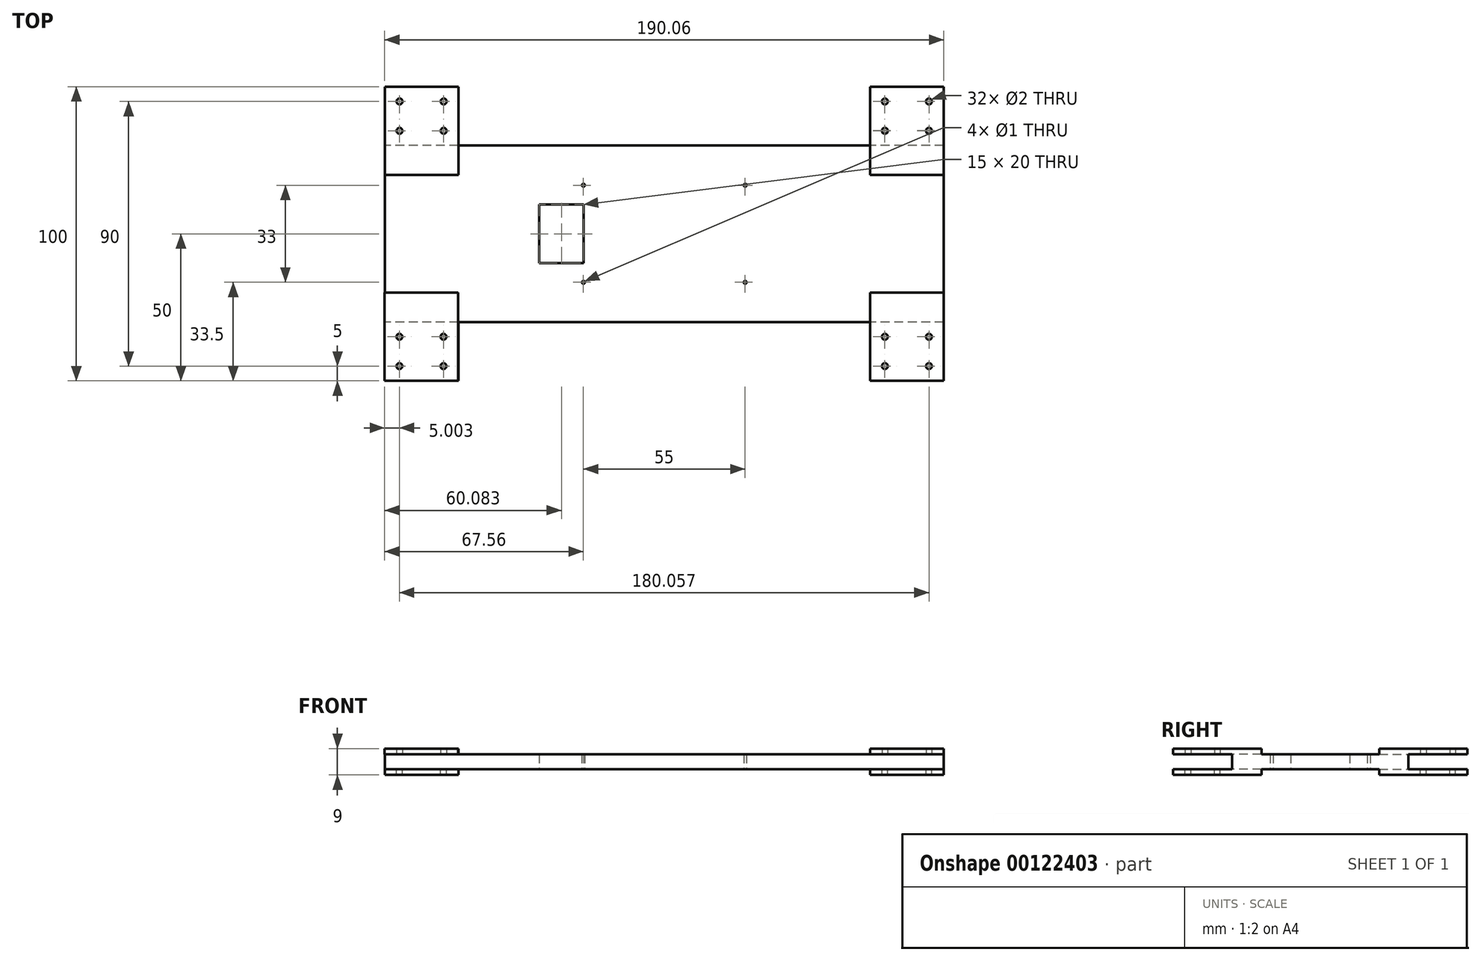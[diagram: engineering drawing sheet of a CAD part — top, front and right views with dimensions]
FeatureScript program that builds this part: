
annotation { "Feature Type Name" : "Feature", "Feature Type Description" : "" }
export const myFeature = defineFeature(function(context is Context, id is Id, definition is map)
    precondition{}
    {
        {
            var Q0;
            Q0=qCreatedBy(makeId("Top.planeOp"),FACE);
            var sketch = newSketch(context, id + "F0", { "sketchPlane" : qUnion([Q0])});
            skLineSegment(sketch, "E0.bottom", {"start": v(95, -30) * mm, "end": v(-95, -30) * mm});
            skLineSegment(sketch, "E0.top", {"start": v(95, 30) * mm, "end": v(-95, 30) * mm});
            skLineSegment(sketch, "E0.left", {"start": v(95, -30) * mm, "end": v(95, 30) * mm});
            skLineSegment(sketch, "E0.right", {"start": v(-95, -30) * mm, "end": v(-95, 30) * mm});
            skPoint(sketch, "E0.middle", {"position": v(0, 0) * mm});
            skLineSegment(sketch, "E1.bottom", {"start": v(27.5, -16.5) * mm, "end": v(-27.5, -16.5) * mm});
            skLineSegment(sketch, "E1.top", {"start": v(27.5, 16.5) * mm, "end": v(-27.5, 16.5) * mm});
            skLineSegment(sketch, "E1.left", {"start": v(27.5, -16.5) * mm, "end": v(27.5, 16.5) * mm});
            skLineSegment(sketch, "E1.right", {"start": v(-27.5, -16.5) * mm, "end": v(-27.5, 16.5) * mm});
            skCircle(sketch, "E2", {"center": v(-27.5, 16.5) * mm, "radius": 0.5 * mm});
            skCircle(sketch, "E3", {"center": v(27.5, 16.5) * mm, "radius": 0.5 * mm});
            skCircle(sketch, "E4", {"center": v(-27.5, -16.5) * mm, "radius": 0.5 * mm});
            skCircle(sketch, "E5", {"center": v(27.5, -16.5) * mm, "radius": 0.5 * mm});
            skLineSegment(sketch, "E6.bottom", {"start": v(-236.35, 48.21) * mm, "end": v(-211.35, 48.21) * mm});
            skLineSegment(sketch, "E6.top", {"start": v(-236.35, 108.21) * mm, "end": v(-211.35, 108.21) * mm});
            skLineSegment(sketch, "E6.left", {"start": v(-236.35, 48.21) * mm, "end": v(-236.35, 108.21) * mm});
            skLineSegment(sketch, "E6.right", {"start": v(-211.35, 48.21) * mm, "end": v(-211.35, 108.21) * mm});
            skLineSegment(sketch, "E7", {"start": v(-223.85, 108.21) * mm, "end": v(-223.85, 48.21) * mm});
            skCircle(sketch, "E8", {"center": v(-223.85, 98.21) * mm, "radius": 3 * mm});
            skCircle(sketch, "E9", {"center": v(-223.85, 98.21) * mm, "radius": 5 * mm});
            skLineSegment(sketch, "E10.bottom", {"start": v(-251.47, -12.81) * mm, "end": v(-331.47, -12.81) * mm});
            skLineSegment(sketch, "E10.top", {"start": v(-251.47, 32.19) * mm, "end": v(-331.47, 32.19) * mm});
            skLineSegment(sketch, "E10.left", {"start": v(-251.47, -12.81) * mm, "end": v(-251.47, 32.19) * mm});
            skLineSegment(sketch, "E10.right", {"start": v(-331.47, -12.81) * mm, "end": v(-331.47, 32.19) * mm});
            skLineSegment(sketch, "E11.bottom", {"start": v(-27.48, 10) * mm, "end": v(-42.48, 10) * mm});
            skLineSegment(sketch, "E11.top", {"start": v(-27.48, -10) * mm, "end": v(-42.48, -10) * mm});
            skLineSegment(sketch, "E11.left", {"start": v(-27.48, 10) * mm, "end": v(-27.48, -10) * mm});
            skLineSegment(sketch, "E11.right", {"start": v(-42.48, 10) * mm, "end": v(-42.48, -10) * mm});
            skSolve(sketch);
        }
        {
            var Q0;
            Q0=makeQuery(id+"F0.imprint","IMPRINT",FACE,{"disambiguationData":[TD([[makeQuery(id+"F0.imprint","IMPRINT",EDGE,{"derivedFrom":sQuery(id+"F0.wireOp",EDGE,"E0.bottom")}),-1.0]])]});
            var Q1;
            {var subQ10=sQuery(id+"F0.wireOp",EDGE,"E5");var subQ13=sQuery(id+"F0.wireOp",EDGE,"E1.bottom");var subQ14=makeQuery(id+"F0.imprint","INTERSECT",VERTEX,{"derivedFrom":[subQ13,subQ10]});Q1=makeQuery(id+"F0.imprint","IMPRINT",FACE,{"disambiguationData":[TD([[makeQuery(id+"F0.imprint","IMPRINT",EDGE,{"disambiguationData":[TD([[subQ14,-1.0]])],"derivedFrom":subQ13}),-1.0]])]});}
            extrude(context, id + "F1", {"entities" : qUnion([Q0, Q1]), "depth" : 5 * mm});
        }
        {
            var Q0;
            Q0=makeQuery(id+"F1.opExtrude","CAP_FACE",FACE,{"disambiguationData":[OSD([sQuery(id+"F0.wireOp",EDGE,"E0.bottom"),sQuery(id+"F0.wireOp",EDGE,"E0.top"),sQuery(id+"F0.wireOp",EDGE,"E0.left"),sQuery(id+"F0.wireOp",EDGE,"E0.right"),sQuery(id+"F0.wireOp",EDGE,"E2"),sQuery(id+"F0.wireOp",EDGE,"E3"),sQuery(id+"F0.wireOp",EDGE,"E4"),sQuery(id+"F0.wireOp",EDGE,"E5")])],"isStart":false});
            var sketch = newSketch(context, id + "F2", { "sketchPlane" : qUnion([Q0])});
            skLineSegment(sketch, "E12.bottom", {"start": v(-95, 20) * mm, "end": v(-70, 20) * mm});
            skLineSegment(sketch, "E12.top", {"start": v(-95, 50) * mm, "end": v(-70, 50) * mm});
            skLineSegment(sketch, "E12.left", {"start": v(-95, 20) * mm, "end": v(-95, 50) * mm});
            skLineSegment(sketch, "E12.right", {"start": v(-70, 20) * mm, "end": v(-70, 50) * mm});
            skLineSegment(sketch, "E13.bottom", {"start": v(-90, 45) * mm, "end": v(-75, 45) * mm});
            skLineSegment(sketch, "E13.top", {"start": v(-90, 35) * mm, "end": v(-75, 35) * mm});
            skLineSegment(sketch, "E13.left", {"start": v(-90, 45) * mm, "end": v(-90, 35) * mm});
            skLineSegment(sketch, "E13.right", {"start": v(-75, 45) * mm, "end": v(-75, 35) * mm});
            skCircle(sketch, "E14", {"center": v(-90, 45) * mm, "radius": 1 * mm});
            skCircle(sketch, "E15", {"center": v(-75, 45) * mm, "radius": 1 * mm});
            skCircle(sketch, "E16", {"center": v(-75, 35) * mm, "radius": 1 * mm});
            skCircle(sketch, "E17", {"center": v(-90, 35) * mm, "radius": 1 * mm});
            skLineSegment(sketch, "E18.bottom", {"start": v(-70.06, -20) * mm, "end": v(-95.06, -20) * mm});
            skLineSegment(sketch, "E18.top", {"start": v(-70.06, -50) * mm, "end": v(-95.06, -50) * mm});
            skLineSegment(sketch, "E18.left", {"start": v(-70.06, -20) * mm, "end": v(-70.06, -50) * mm});
            skLineSegment(sketch, "E18.right", {"start": v(-95.06, -20) * mm, "end": v(-95.06, -50) * mm});
            skLineSegment(sketch, "E19.bottom", {"start": v(-75.06, -45) * mm, "end": v(-90.06, -45) * mm});
            skLineSegment(sketch, "E19.top", {"start": v(-75.06, -35) * mm, "end": v(-90.06, -35) * mm});
            skLineSegment(sketch, "E19.left", {"start": v(-75.06, -45) * mm, "end": v(-75.06, -35) * mm});
            skLineSegment(sketch, "E19.right", {"start": v(-90.06, -45) * mm, "end": v(-90.06, -35) * mm});
            skCircle(sketch, "E20", {"center": v(-75.06, -45) * mm, "radius": 1 * mm});
            skCircle(sketch, "E21", {"center": v(-90.06, -45) * mm, "radius": 1 * mm});
            skCircle(sketch, "E22", {"center": v(-90.06, -35) * mm, "radius": 1 * mm});
            skCircle(sketch, "E23", {"center": v(-75.06, -35) * mm, "radius": 1 * mm});
            skLineSegment(sketch, "E24.bottom", {"start": v(70, 20) * mm, "end": v(95, 20) * mm});
            skLineSegment(sketch, "E24.top", {"start": v(70, 50) * mm, "end": v(95, 50) * mm});
            skLineSegment(sketch, "E24.left", {"start": v(70, 20) * mm, "end": v(70, 50) * mm});
            skLineSegment(sketch, "E24.right", {"start": v(95, 20) * mm, "end": v(95, 50) * mm});
            skLineSegment(sketch, "E25.bottom", {"start": v(75, 45) * mm, "end": v(90, 45) * mm});
            skLineSegment(sketch, "E25.top", {"start": v(75, 35) * mm, "end": v(90, 35) * mm});
            skLineSegment(sketch, "E25.left", {"start": v(75, 45) * mm, "end": v(75, 35) * mm});
            skLineSegment(sketch, "E25.right", {"start": v(90, 45) * mm, "end": v(90, 35) * mm});
            skCircle(sketch, "E26", {"center": v(75, 45) * mm, "radius": 1 * mm});
            skCircle(sketch, "E27", {"center": v(90, 45) * mm, "radius": 1 * mm});
            skCircle(sketch, "E28", {"center": v(90, 35) * mm, "radius": 1 * mm});
            skCircle(sketch, "E29", {"center": v(75, 35) * mm, "radius": 1 * mm});
            skLineSegment(sketch, "E30.bottom", {"start": v(95, -20) * mm, "end": v(70, -20) * mm});
            skLineSegment(sketch, "E30.top", {"start": v(95, -50) * mm, "end": v(70, -50) * mm});
            skLineSegment(sketch, "E30.left", {"start": v(95, -20) * mm, "end": v(95, -50) * mm});
            skLineSegment(sketch, "E30.right", {"start": v(70, -20) * mm, "end": v(70, -50) * mm});
            skLineSegment(sketch, "E31.bottom", {"start": v(90, -45) * mm, "end": v(75, -45) * mm});
            skLineSegment(sketch, "E31.top", {"start": v(90, -35) * mm, "end": v(75, -35) * mm});
            skLineSegment(sketch, "E31.left", {"start": v(90, -45) * mm, "end": v(90, -35) * mm});
            skLineSegment(sketch, "E31.right", {"start": v(75, -45) * mm, "end": v(75, -35) * mm});
            skCircle(sketch, "E32", {"center": v(90, -45) * mm, "radius": 1 * mm});
            skCircle(sketch, "E33", {"center": v(75, -45) * mm, "radius": 1 * mm});
            skCircle(sketch, "E34", {"center": v(75, -35) * mm, "radius": 1 * mm});
            skCircle(sketch, "E35", {"center": v(90, -35) * mm, "radius": 1 * mm});
            skSolve(sketch);
        }
        {
            var Q0;
            {var subQ16=sQuery(id+"F2.wireOp",EDGE,"E12.top");Q0=makeQuery(id+"F2.imprint","IMPRINT",FACE,{"disambiguationData":[TD([[makeQuery(id+"F2.imprint","IMPRINT",EDGE,{"derivedFrom":subQ16}),-1.0]])]});}
            var Q1;
            {var subQ9=sQuery(id+"F2.wireOp",EDGE,"E14");var subQ13=sQuery(id+"F2.wireOp",EDGE,"E13.bottom");var subQ14=makeQuery(id+"F2.imprint","INTERSECT",VERTEX,{"derivedFrom":[subQ13,subQ9]});Q1=makeQuery(id+"F2.imprint","IMPRINT",FACE,{"disambiguationData":[TD([[makeQuery(id+"F2.imprint","IMPRINT",EDGE,{"disambiguationData":[TD([[subQ14,-1.0]])],"derivedFrom":subQ13}),-1.0]])]});}
            var Q2;
            {var subQ0=sQuery(id+"F2.wireOp",EDGE,"E12.bottom");Q2=makeQuery(id+"F2.imprint","IMPRINT",FACE,{"disambiguationData":[TD([[makeQuery(id+"F2.imprint","IMPRINT",EDGE,{"derivedFrom":subQ0}),1.0]])]});}
            var Q3;
            {var subQ7=sQuery(id+"F2.wireOp",EDGE,"E26");var subQ13=sQuery(id+"F2.wireOp",EDGE,"E25.bottom");var subQ14=makeQuery(id+"F2.imprint","INTERSECT",VERTEX,{"derivedFrom":[subQ13,subQ7]});Q3=makeQuery(id+"F2.imprint","IMPRINT",FACE,{"disambiguationData":[TD([[makeQuery(id+"F2.imprint","IMPRINT",EDGE,{"disambiguationData":[TD([[subQ14,-1.0]])],"derivedFrom":subQ13}),-1.0]])]});}
            var Q4;
            {var subQ16=sQuery(id+"F2.wireOp",EDGE,"E24.top");Q4=makeQuery(id+"F2.imprint","IMPRINT",FACE,{"disambiguationData":[TD([[makeQuery(id+"F2.imprint","IMPRINT",EDGE,{"derivedFrom":subQ16}),-1.0]])]});}
            var Q5;
            {var subQ0=sQuery(id+"F2.wireOp",EDGE,"E24.bottom");Q5=makeQuery(id+"F2.imprint","IMPRINT",FACE,{"disambiguationData":[TD([[makeQuery(id+"F2.imprint","IMPRINT",EDGE,{"derivedFrom":subQ0}),1.0]])]});}
            var Q6;
            {var subQ6=sQuery(id+"F2.wireOp",EDGE,"E30.top");Q6=makeQuery(id+"F2.imprint","IMPRINT",FACE,{"disambiguationData":[TD([[makeQuery(id+"F2.imprint","IMPRINT",EDGE,{"derivedFrom":subQ6}),-1.0]])]});}
            var Q7;
            {var subQ0=sQuery(id+"F2.wireOp",EDGE,"E32");var subQ13=sQuery(id+"F2.wireOp",EDGE,"E31.bottom");var subQ14=makeQuery(id+"F2.imprint","INTERSECT",VERTEX,{"derivedFrom":[subQ13,subQ0]});Q7=makeQuery(id+"F2.imprint","IMPRINT",FACE,{"disambiguationData":[TD([[makeQuery(id+"F2.imprint","IMPRINT",EDGE,{"disambiguationData":[TD([[subQ14,-1.0]])],"derivedFrom":subQ13}),-1.0]])]});}
            var Q8;
            {var subQ0=sQuery(id+"F2.wireOp",EDGE,"E30.bottom");Q8=makeQuery(id+"F2.imprint","IMPRINT",FACE,{"disambiguationData":[TD([[makeQuery(id+"F2.imprint","IMPRINT",EDGE,{"derivedFrom":subQ0}),1.0]])]});}
            var Q9;
            {var subQ0=sQuery(id+"F2.wireOp",EDGE,"E18.left");var subQ1=sQuery(id+"F2.wireOp",EDGE,"E18.bottom");var subQ2=makeQuery(id+"F2.imprint","INTERSECT",VERTEX,{"derivedFrom":[subQ1,subQ0]});Q9=makeQuery(id+"F2.imprint","IMPRINT",FACE,{"disambiguationData":[TD([[makeQuery(id+"F2.imprint","IMPRINT",EDGE,{"disambiguationData":[TD([[subQ2,-1.0]])],"derivedFrom":subQ1}),1.0]])]});}
            var Q10;
            {var subQ20=sQuery(id+"F2.wireOp",EDGE,"E18.top");Q10=makeQuery(id+"F2.imprint","IMPRINT",FACE,{"disambiguationData":[TD([[makeQuery(id+"F2.imprint","IMPRINT",EDGE,{"derivedFrom":subQ20}),-1.0]])]});}
            var Q11;
            {var subQ0=sQuery(id+"F2.wireOp",EDGE,"E20");var subQ5=sQuery(id+"F2.wireOp",EDGE,"E19.bottom");var subQ6=makeQuery(id+"F2.imprint","INTERSECT",VERTEX,{"derivedFrom":[subQ5,subQ0]});Q11=makeQuery(id+"F2.imprint","IMPRINT",FACE,{"disambiguationData":[TD([[makeQuery(id+"F2.imprint","IMPRINT",EDGE,{"disambiguationData":[TD([[subQ6,-1.0]])],"derivedFrom":subQ5}),-1.0]])]});}
            extrude(context, id + "F3", {"entities" : qUnion([Q0, Q1, Q2, Q3, Q4, Q5, Q6, Q7, Q8, Q9, Q10, Q11]), "operationType" : NewBodyOperationType.ADD, "depth" : 2 * mm});
        }
        {
            var Q0;
            Q0=makeQuery(id+"F1.opExtrude","CAP_FACE",FACE,{"disambiguationData":[OSD([sQuery(id+"F0.wireOp",EDGE,"E0.bottom"),sQuery(id+"F0.wireOp",EDGE,"E0.top"),sQuery(id+"F0.wireOp",EDGE,"E0.left"),sQuery(id+"F0.wireOp",EDGE,"E0.right"),sQuery(id+"F0.wireOp",EDGE,"E2"),sQuery(id+"F0.wireOp",EDGE,"E3"),sQuery(id+"F0.wireOp",EDGE,"E4"),sQuery(id+"F0.wireOp",EDGE,"E5")])],"isStart":true});
            var sketch = newSketch(context, id + "F4", { "sketchPlane" : qUnion([Q0])});
            skLineSegment(sketch, "E36.bottom", {"start": v(-95, 20) * mm, "end": v(-70, 20) * mm});
            skLineSegment(sketch, "E36.top", {"start": v(-95, 50) * mm, "end": v(-70, 50) * mm});
            skLineSegment(sketch, "E36.left", {"start": v(-95, 20) * mm, "end": v(-95, 50) * mm});
            skLineSegment(sketch, "E36.right", {"start": v(-70, 20) * mm, "end": v(-70, 50) * mm});
            skLineSegment(sketch, "E37.bottom", {"start": v(-90, 45) * mm, "end": v(-75, 45) * mm});
            skLineSegment(sketch, "E37.top", {"start": v(-90, 35) * mm, "end": v(-75, 35) * mm});
            skLineSegment(sketch, "E37.left", {"start": v(-90, 45) * mm, "end": v(-90, 35) * mm});
            skLineSegment(sketch, "E37.right", {"start": v(-75, 45) * mm, "end": v(-75, 35) * mm});
            skCircle(sketch, "E38", {"center": v(-90, 45) * mm, "radius": 1 * mm});
            skCircle(sketch, "E39", {"center": v(-75, 45) * mm, "radius": 1 * mm});
            skCircle(sketch, "E40", {"center": v(-75, 35) * mm, "radius": 1 * mm});
            skCircle(sketch, "E41", {"center": v(-90, 35) * mm, "radius": 1 * mm});
            skLineSegment(sketch, "E42.bottom", {"start": v(70, 20) * mm, "end": v(95, 20) * mm});
            skLineSegment(sketch, "E42.top", {"start": v(70, 50) * mm, "end": v(95, 50) * mm});
            skLineSegment(sketch, "E42.left", {"start": v(70, 20) * mm, "end": v(70, 50) * mm});
            skLineSegment(sketch, "E42.right", {"start": v(95, 20) * mm, "end": v(95, 50) * mm});
            skLineSegment(sketch, "E43.bottom", {"start": v(75, 45) * mm, "end": v(90, 45) * mm});
            skLineSegment(sketch, "E43.top", {"start": v(75, 35) * mm, "end": v(90, 35) * mm});
            skLineSegment(sketch, "E43.left", {"start": v(75, 45) * mm, "end": v(75, 35) * mm});
            skLineSegment(sketch, "E43.right", {"start": v(90, 45) * mm, "end": v(90, 35) * mm});
            skCircle(sketch, "E44", {"center": v(75, 45) * mm, "radius": 1 * mm});
            skCircle(sketch, "E45", {"center": v(90, 45) * mm, "radius": 1 * mm});
            skCircle(sketch, "E46", {"center": v(90, 35) * mm, "radius": 1 * mm});
            skCircle(sketch, "E47", {"center": v(75, 35) * mm, "radius": 1 * mm});
            skLineSegment(sketch, "E48.bottom", {"start": v(-70, -20) * mm, "end": v(-95, -20) * mm});
            skLineSegment(sketch, "E48.top", {"start": v(-70, -50) * mm, "end": v(-95, -50) * mm});
            skLineSegment(sketch, "E48.left", {"start": v(-70, -20) * mm, "end": v(-70, -50) * mm});
            skLineSegment(sketch, "E48.right", {"start": v(-95, -20) * mm, "end": v(-95, -50) * mm});
            skLineSegment(sketch, "E49.bottom", {"start": v(-75, -45) * mm, "end": v(-90, -45) * mm});
            skLineSegment(sketch, "E49.top", {"start": v(-75, -35) * mm, "end": v(-90, -35) * mm});
            skLineSegment(sketch, "E49.left", {"start": v(-75, -45) * mm, "end": v(-75, -35) * mm});
            skLineSegment(sketch, "E49.right", {"start": v(-90, -45) * mm, "end": v(-90, -35) * mm});
            skCircle(sketch, "E50", {"center": v(-75, -45) * mm, "radius": 1 * mm});
            skCircle(sketch, "E51", {"center": v(-90, -45) * mm, "radius": 1 * mm});
            skCircle(sketch, "E52", {"center": v(-90, -35) * mm, "radius": 1 * mm});
            skCircle(sketch, "E53", {"center": v(-75, -35) * mm, "radius": 1 * mm});
            skLineSegment(sketch, "E54.bottom", {"start": v(95, -20) * mm, "end": v(70, -20) * mm});
            skLineSegment(sketch, "E54.top", {"start": v(95, -50) * mm, "end": v(70, -50) * mm});
            skLineSegment(sketch, "E54.left", {"start": v(95, -20) * mm, "end": v(95, -50) * mm});
            skLineSegment(sketch, "E54.right", {"start": v(70, -20) * mm, "end": v(70, -50) * mm});
            skLineSegment(sketch, "E55.bottom", {"start": v(90, -45) * mm, "end": v(75, -45) * mm});
            skLineSegment(sketch, "E55.top", {"start": v(90, -35.07) * mm, "end": v(75, -35.07) * mm});
            skLineSegment(sketch, "E55.left", {"start": v(90, -45) * mm, "end": v(90, -35.07) * mm});
            skLineSegment(sketch, "E55.right", {"start": v(75, -45) * mm, "end": v(75, -35.07) * mm});
            skCircle(sketch, "E56", {"center": v(90, -45) * mm, "radius": 1 * mm});
            skCircle(sketch, "E57", {"center": v(75, -45) * mm, "radius": 1 * mm});
            skCircle(sketch, "E58", {"center": v(75, -35.07) * mm, "radius": 1 * mm});
            skCircle(sketch, "E59", {"center": v(90, -35.07) * mm, "radius": 1 * mm});
            skSolve(sketch);
        }
        {
            var Q0;
            {var subQ0=sQuery(id+"F4.wireOp",EDGE,"E38");var subQ13=sQuery(id+"F4.wireOp",EDGE,"E37.bottom");var subQ14=makeQuery(id+"F4.imprint","INTERSECT",VERTEX,{"derivedFrom":[subQ13,subQ0]});Q0=makeQuery(id+"F4.imprint","IMPRINT",FACE,{"disambiguationData":[TD([[makeQuery(id+"F4.imprint","IMPRINT",EDGE,{"disambiguationData":[TD([[subQ14,-1.0]])],"derivedFrom":subQ13}),-1.0]])]});}
            var Q1;
            {var subQ13=sQuery(id+"F4.wireOp",EDGE,"E36.top");Q1=makeQuery(id+"F4.imprint","IMPRINT",FACE,{"disambiguationData":[TD([[makeQuery(id+"F4.imprint","IMPRINT",EDGE,{"derivedFrom":subQ13}),-1.0]])]});}
            var Q2;
            {var subQ0=sQuery(id+"F4.wireOp",EDGE,"E36.bottom");Q2=makeQuery(id+"F4.imprint","IMPRINT",FACE,{"disambiguationData":[TD([[makeQuery(id+"F4.imprint","IMPRINT",EDGE,{"derivedFrom":subQ0}),1.0]])]});}
            var Q3;
            {var subQ5=sQuery(id+"F4.wireOp",EDGE,"E44");var subQ10=sQuery(id+"F4.wireOp",EDGE,"E43.bottom");var subQ11=makeQuery(id+"F4.imprint","INTERSECT",VERTEX,{"derivedFrom":[subQ10,subQ5]});Q3=makeQuery(id+"F4.imprint","IMPRINT",FACE,{"disambiguationData":[TD([[makeQuery(id+"F4.imprint","IMPRINT",EDGE,{"disambiguationData":[TD([[subQ11,-1.0]])],"derivedFrom":subQ10}),-1.0]])]});}
            var Q4;
            {var subQ15=sQuery(id+"F4.wireOp",EDGE,"E42.top");Q4=makeQuery(id+"F4.imprint","IMPRINT",FACE,{"disambiguationData":[TD([[makeQuery(id+"F4.imprint","IMPRINT",EDGE,{"derivedFrom":subQ15}),-1.0]])]});}
            var Q5;
            {var subQ0=sQuery(id+"F4.wireOp",EDGE,"E42.bottom");Q5=makeQuery(id+"F4.imprint","IMPRINT",FACE,{"disambiguationData":[TD([[makeQuery(id+"F4.imprint","IMPRINT",EDGE,{"derivedFrom":subQ0}),1.0]])]});}
            var Q6;
            {var subQ0=sQuery(id+"F4.wireOp",EDGE,"E54.bottom");Q6=makeQuery(id+"F4.imprint","IMPRINT",FACE,{"disambiguationData":[TD([[makeQuery(id+"F4.imprint","IMPRINT",EDGE,{"derivedFrom":subQ0}),1.0]])]});}
            var Q7;
            {var subQ19=sQuery(id+"F4.wireOp",EDGE,"E54.top");Q7=makeQuery(id+"F4.imprint","IMPRINT",FACE,{"disambiguationData":[TD([[makeQuery(id+"F4.imprint","IMPRINT",EDGE,{"derivedFrom":subQ19}),-1.0]])]});}
            var Q8;
            {var subQ0=sQuery(id+"F4.wireOp",EDGE,"E56");var subQ5=sQuery(id+"F4.wireOp",EDGE,"E55.bottom");var subQ6=makeQuery(id+"F4.imprint","INTERSECT",VERTEX,{"derivedFrom":[subQ5,subQ0]});Q8=makeQuery(id+"F4.imprint","IMPRINT",FACE,{"disambiguationData":[TD([[makeQuery(id+"F4.imprint","IMPRINT",EDGE,{"disambiguationData":[TD([[subQ6,-1.0]])],"derivedFrom":subQ5}),-1.0]])]});}
            var Q9;
            {var subQ0=sQuery(id+"F4.wireOp",EDGE,"E48.bottom");Q9=makeQuery(id+"F4.imprint","IMPRINT",FACE,{"disambiguationData":[TD([[makeQuery(id+"F4.imprint","IMPRINT",EDGE,{"derivedFrom":subQ0}),1.0]])]});}
            var Q10;
            {var subQ5=sQuery(id+"F4.wireOp",EDGE,"E50");var subQ13=sQuery(id+"F4.wireOp",EDGE,"E49.bottom");var subQ14=makeQuery(id+"F4.imprint","INTERSECT",VERTEX,{"derivedFrom":[subQ13,subQ5]});Q10=makeQuery(id+"F4.imprint","IMPRINT",FACE,{"disambiguationData":[TD([[makeQuery(id+"F4.imprint","IMPRINT",EDGE,{"disambiguationData":[TD([[subQ14,-1.0]])],"derivedFrom":subQ13}),-1.0]])]});}
            var Q11;
            {var subQ5=sQuery(id+"F4.wireOp",EDGE,"E48.top");Q11=makeQuery(id+"F4.imprint","IMPRINT",FACE,{"disambiguationData":[TD([[makeQuery(id+"F4.imprint","IMPRINT",EDGE,{"derivedFrom":subQ5}),-1.0]])]});}
            extrude(context, id + "F5", {"entities" : qUnion([Q0, Q1, Q2, Q3, Q4, Q5, Q6, Q7, Q8, Q9, Q10, Q11]), "operationType" : NewBodyOperationType.ADD, "depth" : 2 * mm});
        }
    });
